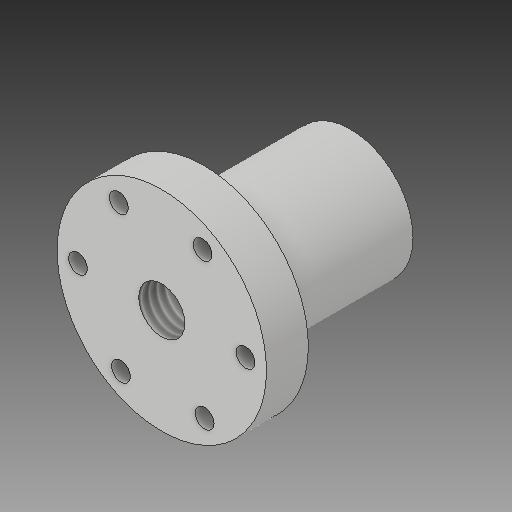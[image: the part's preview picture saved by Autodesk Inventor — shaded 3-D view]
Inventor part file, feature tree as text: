
AUTODESK INVENTOR PART (.ipt)
format: ipt  version: 2018 (Build 220112000, 112)  size: 137,216 bytes
history: native  units: mm
features: sketch x3, extrude x2, revolve x1, thread x1
ambient origin geometry x8: Origin, YZ Plane, XZ Plane, XY Plane, X Axis, Y Axis, Z Axis, Center Point
bodies: Solid1 (feature_tree)
feature tree (7):
  revolve  "Revolution1"  [1 undecoded]
  extrude  "Extrusion1"  Depth=35.0mm
  extrude  "Extrusion2"  TaperAngle=90.0deg  [1 undecoded]
  thread  "Thread1"  [1 undecoded]
  sketch  "Sketch1"  dims[d3=25.0mm d4=10.0mm]
  sketch  "Sketch2"  dims[d5=10.0mm d6=35.0mm]
  sketch  "Sketch3"  dims[d7=15.0mm d8=90.0deg d12=4.5mm d13=60.0mm d15=360.0deg d17=10.0mm d18=0.0mm d19=11.0mm d27=10.0mm d28=0.0mm d29=10.0mm d30=0.0mm]
note: 3 required parameter values undecoded (feature->parameter linkage not recoverable at this tier; creation-order binding heuristic only, values carry confidence <= 0.55)